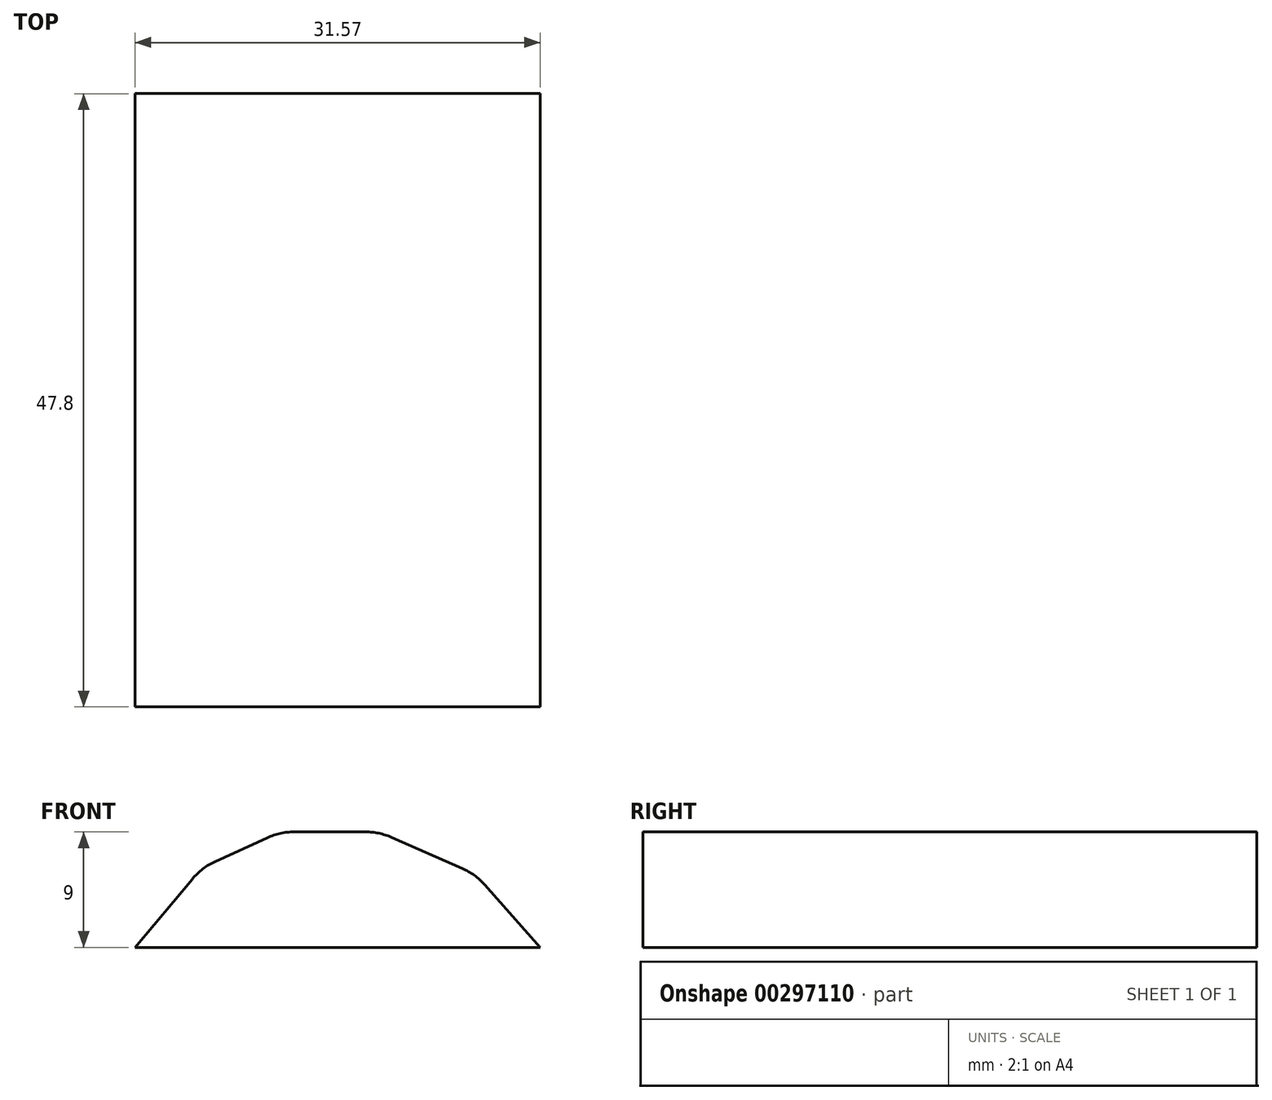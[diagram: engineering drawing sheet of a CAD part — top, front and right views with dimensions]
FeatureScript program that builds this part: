
annotation { "Feature Type Name" : "Feature", "Feature Type Description" : "" }
export const myFeature = defineFeature(function(context is Context, id is Id, definition is map)
    precondition{}
    {
        {
            var Q0;
            Q0=qCreatedBy(makeId("Top.planeOp"),FACE);
            var sketch = newSketch(context, id + "F0", { "sketchPlane" : qUnion([Q0])});
            skLineSegment(sketch, "E0.bottom", {"start": v(1.01, 0) * mm, "end": v(36.01, 0) * mm});
            skLineSegment(sketch, "E0.top", {"start": v(1.01, 47.8) * mm, "end": v(36.01, 47.8) * mm});
            skLineSegment(sketch, "E0.left", {"start": v(1.01, 0) * mm, "end": v(1.01, 47.8) * mm});
            skLineSegment(sketch, "E0.right", {"start": v(36.01, 0) * mm, "end": v(36.01, 47.8) * mm});
            skLineSegment(sketch, "E1.bottom", {"start": v(118.68, 29.92) * mm, "end": v(113.61, 29.92) * mm});
            skLineSegment(sketch, "E1.top", {"start": v(118.68, 36.14) * mm, "end": v(113.61, 36.14) * mm});
            skLineSegment(sketch, "E1.left", {"start": v(118.68, 29.92) * mm, "end": v(118.68, 36.14) * mm});
            skLineSegment(sketch, "E1.right", {"start": v(113.61, 29.92) * mm, "end": v(113.61, 36.14) * mm});
            skSolve(sketch);
        }
        {
            var Q0;
            Q0=makeQuery(id+"F0.imprint","IMPRINT",FACE,{"disambiguationData":[TD([[makeQuery(id+"F0.imprint","IMPRINT",EDGE,{"derivedFrom":sQuery(id+"F0.wireOp",EDGE,"E0.bottom")}),1.0]])]});
            extrude(context, id + "F1", {"entities" : qUnion([Q0]), "depth" : 24.64 * mm});
        }
        {
            var Q0;
            Q0=makeQuery(id+"F1.opExtrude","SWEPT_FACE",FACE,{"disambiguationData":[OSD([sQuery(id+"F0.wireOp",EDGE,"E0.top")])]});
            var sketch = newSketch(context, id + "F2", { "sketchPlane" : qUnion([Q0])});
            skLineSegment(sketch, "E2", {"start": v(-36.01, 0) * mm, "end": v(-30.94, 5.7) * mm});
            skLineSegment(sketch, "E3", {"start": v(-30.94, 5.7) * mm, "end": v(-23.46, 9) * mm});
            skLineSegment(sketch, "E4", {"start": v(-23.46, 9) * mm, "end": v(-15.72, 9) * mm});
            skLineSegment(sketch, "E5", {"start": v(-15.72, 9) * mm, "end": v(-9.64, 6.21) * mm});
            skLineSegment(sketch, "E6", {"start": v(-9.64, 6.21) * mm, "end": v(-4.44, 0) * mm});
            skSolve(sketch);
        }
        {
            var Q0;
            Q0 = qSketchRegion(id + "F2", true);
            var Q1;
            Q1=makeQuery(id+"F2.imprint","IMPRINT",FACE,{"disambiguationData":[TD([[makeQuery(id+"F2.imprint","IMPRINT",EDGE,{"derivedFrom":sQuery(id+"F2.wireOp",EDGE,"E2")}),1.0]])]});
            extrude(context, id + "F3", {"entities" : qUnion([Q0, Q1]), "operationType" : NewBodyOperationType.ADD, "depth" : 25.4 * mm});
        }
        {
            var Q0;
            Q0=makeQuery(id+"F3.opExtrude","CAP_FACE",FACE,{"disambiguationData":[OSD([sQuery(id+"F0.wireOp",EDGE,"E0.top"),sQuery(id+"F0.wireOp",EDGE,"E0.left"),sQuery(id+"F0.wireOp",EDGE,"E0.right"),sQuery(id+"F2.wireOp",EDGE,"E2"),sQuery(id+"F2.wireOp",EDGE,"E3"),sQuery(id+"F2.wireOp",EDGE,"E4"),sQuery(id+"F2.wireOp",EDGE,"E5"),sQuery(id+"F2.wireOp",EDGE,"E6")])],"isStart":false});
            extrude(context, id + "F4", {"entities" : qUnion([Q0]), "operationType" : NewBodyOperationType.REMOVE, "oppositeDirection" : true, "depth" : 89.4 * mm});
        }
        {
            var Q0;
            Q0=makeQuery(id+"F4.boolean.opBoolean","COPY",EDGE,{"derivedFrom":makeQuery(id+"F4.opExtrude","SWEPT_EDGE",EDGE,{"disambiguationData":[OSD([sQuery(id+"F2.wireOp",EDGE,"E3"),sQuery(id+"F2.wireOp",EDGE,"E4")])]})});
            fillet(context, id + "F5", {"entities" : qUnion([Q0]), "radius" : 5.08 * mm, "tangentPropagation" : true, "allowEdgeOverflow" : false});
        }
        {
            var Q0;
            Q0=makeQuery(id+"F4.boolean.opBoolean","COPY",EDGE,{"derivedFrom":makeQuery(id+"F4.opExtrude","SWEPT_EDGE",EDGE,{"disambiguationData":[OSD([sQuery(id+"F2.wireOp",EDGE,"E4"),sQuery(id+"F2.wireOp",EDGE,"E5")])]})});
            var Q1;
            Q1=makeQuery(id+"F4.boolean.opBoolean","COPY",EDGE,{"derivedFrom":makeQuery(id+"F4.opExtrude","SWEPT_EDGE",EDGE,{"disambiguationData":[OSD([sQuery(id+"F2.wireOp",EDGE,"E5"),sQuery(id+"F2.wireOp",EDGE,"E6")])]})});
            var Q2;
            Q2=makeQuery(id+"F4.boolean.opBoolean","COPY",EDGE,{"derivedFrom":makeQuery(id+"F4.opExtrude","SWEPT_EDGE",EDGE,{"disambiguationData":[OSD([sQuery(id+"F2.wireOp",EDGE,"E2"),sQuery(id+"F2.wireOp",EDGE,"E3")])]})});
            fillet(context, id + "F6", {"entities" : qUnion([Q0, Q1, Q2]), "radius" : 5.08 * mm, "tangentPropagation" : true, "allowEdgeOverflow" : false});
        }
    });
